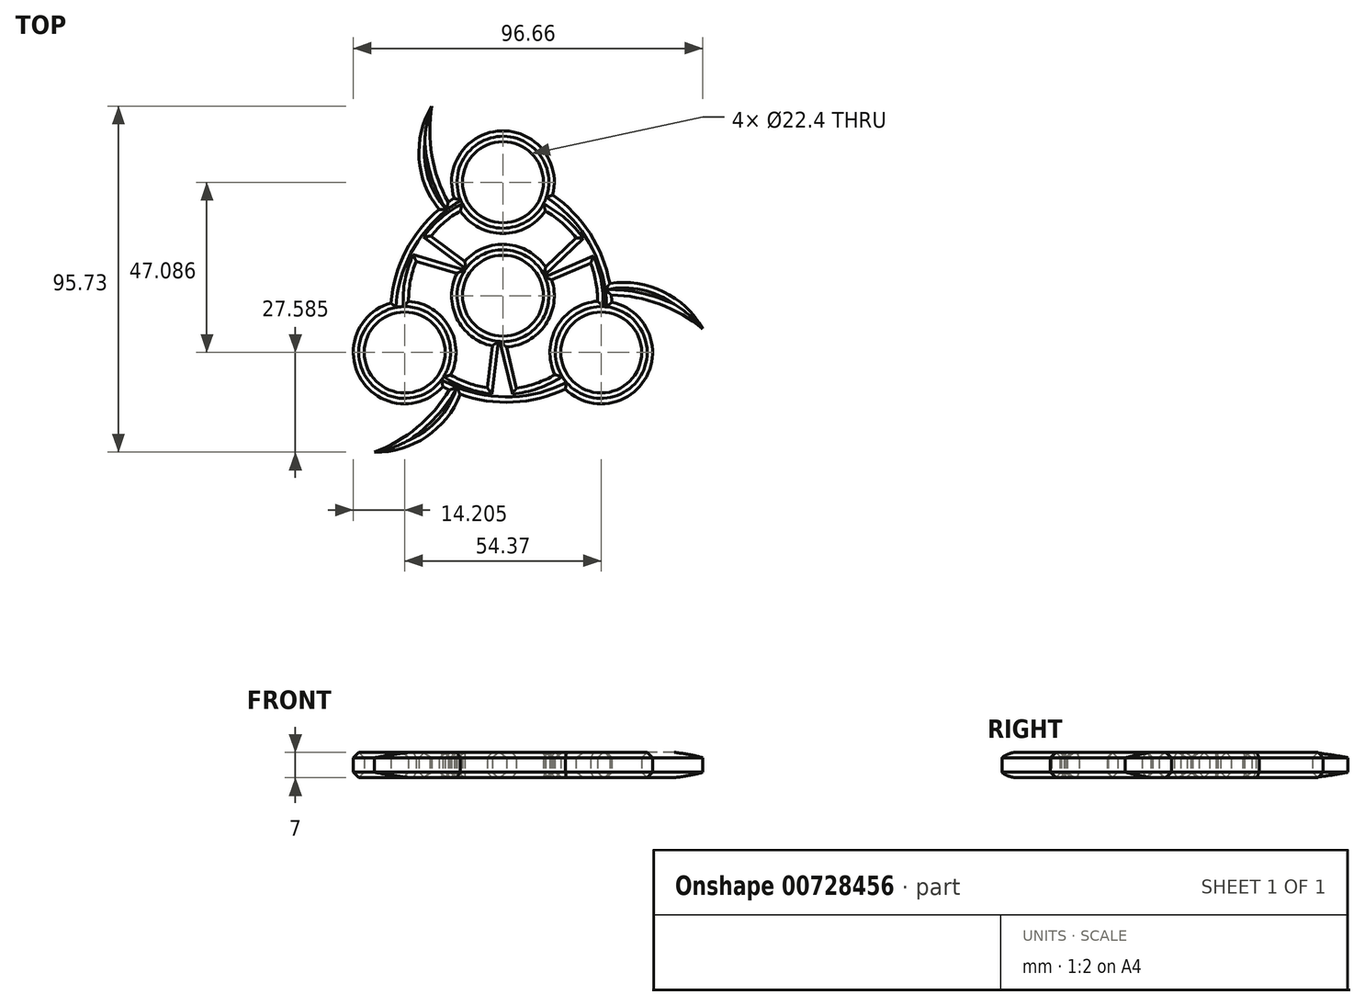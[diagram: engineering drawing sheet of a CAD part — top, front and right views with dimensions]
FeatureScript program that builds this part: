
annotation { "Feature Type Name" : "Feature", "Feature Type Description" : "" }
export const myFeature = defineFeature(function(context is Context, id is Id, definition is map)
    precondition{}
    {
        {
            var Q0;
            Q0=qCreatedBy(makeId("Top.planeOp"),FACE);
            var sketch = newSketch(context, id + "F0", { "sketchPlane" : qUnion([Q0])});
            skCircle(sketch, "E0", {"center": v(0, 0) * mm, "radius": 11.2 * mm});
            skArc(sketch, "E1", {"start": v(-12.76, 6.23) * mm, "mid": v(-12.77, -6.2) * mm, "end": v(-2.98, -13.88) * mm});
            skCircle(sketch, "E2", {"center": v(0, 31.4) * mm, "radius": 11.2 * mm});
            skArc(sketch, "E3", {"start": v(-11.77, 23.45) * mm, "mid": v(-0.04, 17.2) * mm, "end": v(11.72, 23.38) * mm});
            skCircle(sketch, "E4.1.0", {"center": v(-27.19, -15.7) * mm, "radius": 11.2 * mm});
            skArc(sketch, "E4.1.1", {"start": v(-14.42, -21.92) * mm, "mid": v(-14.87, -8.63) * mm, "end": v(-26.11, -1.54) * mm});
            skCircle(sketch, "E4.2.0", {"center": v(27.19, -15.7) * mm, "radius": 11.2 * mm});
            skArc(sketch, "E4.2.1", {"start": v(17.24, -25.83) * mm, "mid": v(38.73, -7.43) * mm, "end": v(14.39, -21.84) * mm});
            skArc(sketch, "E5", {"start": v(30.1, -1.8) * mm, "mid": v(30.05, -0.8) * mm, "end": v(29.97, 0.2) * mm});
            skArc(sketch, "E6", {"start": v(26.2, -1.53) * mm, "mid": v(22.35, 12.9) * mm, "end": v(11.72, 23.38) * mm});
            skArc(sketch, "E7.1.0", {"start": v(-11.77, 23.45) * mm, "mid": v(-22.34, 12.9) * mm, "end": v(-26.11, -1.54) * mm});
            skArc(sketch, "E7.1.1", {"start": v(-13.5, 26.97) * mm, "mid": v(-14.33, 26.43) * mm, "end": v(-15.15, 25.86) * mm});
            skArc(sketch, "E7.2.0", {"start": v(-14.42, -21.92) * mm, "mid": v(0, -25.8) * mm, "end": v(14.39, -21.84) * mm});
            skArc(sketch, "E7.2.1", {"start": v(-16.61, -25.18) * mm, "mid": v(-15.72, -25.63) * mm, "end": v(-14.82, -26.05) * mm});
            skLineSegment(sketch, "E8", {"start": v(-19.89, 16.5) * mm, "end": v(-10.53, 9.53) * mm});
            skLineSegment(sketch, "E9", {"start": v(-10.53, 9.53) * mm, "end": v(-12.76, 6.23) * mm});
            skLineSegment(sketch, "E10", {"start": v(-12.76, 6.23) * mm, "end": v(-24, 9.53) * mm});
            skLineSegment(sketch, "E11.1.0", {"start": v(-4.35, -25.48) * mm, "end": v(-2.98, -13.88) * mm});
            skLineSegment(sketch, "E11.1.1", {"start": v(0.98, -14.17) * mm, "end": v(3.75, -25.54) * mm});
            skLineSegment(sketch, "E11.2.0", {"start": v(24.24, 8.97) * mm, "end": v(13.51, 4.36) * mm});
            skLineSegment(sketch, "E11.2.1", {"start": v(11.78, 7.94) * mm, "end": v(20.25, 16.02) * mm});
            skArc(sketch, "E12.trimOffspring", {"start": v(11.78, 7.94) * mm, "mid": v(1, 14.16) * mm, "end": v(-10.53, 9.53) * mm});
            skArc(sketch, "E13.trimOffspring", {"start": v(0.98, -14.17) * mm, "mid": v(11.76, -7.96) * mm, "end": v(13.51, 4.36) * mm});
            skArc(sketch, "E14.trimOffspring", {"start": v(-31, -2.02) * mm, "mid": v(-39.25, -23.19) * mm, "end": v(-16.61, -25.18) * mm});
            skArc(sketch, "E15.trimOffspring", {"start": v(13.75, 27.85) * mm, "mid": v(-0.46, 45.58) * mm, "end": v(-13.5, 26.97) * mm});
            skArc(sketch, "E16", {"start": v(-19.69, 52.45) * mm, "mid": v(-23.19, 37.85) * mm, "end": v(-17.68, 23.9) * mm});
            skArc(sketch, "E17", {"start": v(-19.69, 52.45) * mm, "mid": v(-19.67, 38.77) * mm, "end": v(-15.15, 25.86) * mm});
            skArc(sketch, "E18.1.0", {"start": v(-35.58, -43.28) * mm, "mid": v(-21.19, -39) * mm, "end": v(-11.85, -27.25) * mm});
            skArc(sketch, "E18.1.1", {"start": v(-35.58, -43.28) * mm, "mid": v(-23.74, -36.42) * mm, "end": v(-14.82, -26.05) * mm});
            skArc(sketch, "E18.2.0", {"start": v(55.27, -9.18) * mm, "mid": v(44.38, 1.15) * mm, "end": v(29.53, 3.36) * mm});
            skArc(sketch, "E18.2.1", {"start": v(55.27, -9.18) * mm, "mid": v(43.41, -2.35) * mm, "end": v(29.97, 0.2) * mm});
            skArc(sketch, "E19.trimOffspring", {"start": v(-17.68, 23.9) * mm, "mid": v(-26.9, 12.26) * mm, "end": v(-31, -2.02) * mm});
            skArc(sketch, "E20.trimOffspring", {"start": v(-11.85, -27.25) * mm, "mid": v(2.84, -29.43) * mm, "end": v(17.24, -25.83) * mm});
            skArc(sketch, "E21.trimOffspring", {"start": v(29.53, 3.36) * mm, "mid": v(24.07, 17.17) * mm, "end": v(13.75, 27.85) * mm});
            skSolve(sketch);
        }
        {
            var Q0;
            {var subQ0=sQuery(id+"F0.wireOp",EDGE,"E7.1.0");Q0=makeQuery(id+"F0.imprint","IMPRINT",FACE,{"disambiguationData":[TD([[makeQuery(id+"F0.imprint","IMPRINT",EDGE,{"derivedFrom":subQ0}),-1.0]])]});}
            var Q1;
            {var subQ0=sQuery(id+"F0.wireOp",EDGE,"E5");Q1=makeQuery(id+"F0.imprint","IMPRINT",FACE,{"disambiguationData":[TD([[makeQuery(id+"F0.imprint","IMPRINT",EDGE,{"derivedFrom":subQ0}),1.0]])]});}
            var Q2;
            {var subQ0=sQuery(id+"F0.wireOp",EDGE,"E7.2.0");Q2=makeQuery(id+"F0.imprint","IMPRINT",FACE,{"disambiguationData":[TD([[makeQuery(id+"F0.imprint","IMPRINT",EDGE,{"derivedFrom":subQ0}),-1.0]])]});}
            var Q3;
            Q3=makeQuery(id+"F0.imprint","IMPRINT",FACE,{"disambiguationData":[TD([[makeQuery(id+"F0.imprint","IMPRINT",EDGE,{"derivedFrom":sQuery(id+"F0.wireOp",EDGE,"E4.2.0")}),-1.0]])]});
            var Q4;
            Q4=makeQuery(id+"F0.imprint","IMPRINT",FACE,{"disambiguationData":[TD([[makeQuery(id+"F0.imprint","IMPRINT",EDGE,{"derivedFrom":sQuery(id+"F0.wireOp",EDGE,"E4.1.0")}),-1.0]])]});
            var Q5;
            Q5=makeQuery(id+"F0.imprint","IMPRINT",FACE,{"disambiguationData":[TD([[makeQuery(id+"F0.imprint","IMPRINT",EDGE,{"derivedFrom":sQuery(id+"F0.wireOp",EDGE,"E2")}),-1.0]])]});
            var Q6;
            Q6=makeQuery(id+"F0.imprint","IMPRINT",FACE,{"disambiguationData":[TD([[makeQuery(id+"F0.imprint","IMPRINT",EDGE,{"derivedFrom":sQuery(id+"F0.wireOp",EDGE,"E0")}),-1.0]])]});
            var Q7;
            {var subQ1=sQuery(id+"F0.wireOp",EDGE,"E8");Q7=makeQuery(id+"F0.imprint","IMPRINT",FACE,{"disambiguationData":[TD([[makeQuery(id+"F0.imprint","IMPRINT",EDGE,{"derivedFrom":subQ1}),-1.0]])]});}
            var Q8;
            {var subQ0=sQuery(id+"F0.wireOp",EDGE,"E11.2.0");Q8=makeQuery(id+"F0.imprint","IMPRINT",FACE,{"disambiguationData":[TD([[makeQuery(id+"F0.imprint","IMPRINT",EDGE,{"derivedFrom":subQ0}),-1.0]])]});}
            var Q9;
            {var subQ0=sQuery(id+"F0.wireOp",EDGE,"E11.1.0");Q9=makeQuery(id+"F0.imprint","IMPRINT",FACE,{"disambiguationData":[TD([[makeQuery(id+"F0.imprint","IMPRINT",EDGE,{"derivedFrom":subQ0}),-1.0]])]});}
            extrude(context, id + "F1", {"entities" : qUnion([Q0, Q1, Q2, Q3, Q4, Q5, Q6, Q7, Q8, Q9]), "depth" : 7 * mm, "offsetDistance" : 25 * mm});
        }
        {
            var Q0;
            Q0=makeQuery(id+"F1.opExtrude","CAP_FACE",FACE,{"disambiguationData":[OSD([sQuery(id+"F0.wireOp",EDGE,"E0"),sQuery(id+"F0.wireOp",EDGE,"E1"),sQuery(id+"F0.wireOp",EDGE,"E2"),sQuery(id+"F0.wireOp",EDGE,"E3"),sQuery(id+"F0.wireOp",EDGE,"E4.1.0"),sQuery(id+"F0.wireOp",EDGE,"E4.1.1"),sQuery(id+"F0.wireOp",EDGE,"E4.2.0"),sQuery(id+"F0.wireOp",EDGE,"E4.2.1"),sQuery(id+"F0.wireOp",EDGE,"E5"),sQuery(id+"F0.wireOp",EDGE,"E6"),sQuery(id+"F0.wireOp",EDGE,"E7.1.0"),sQuery(id+"F0.wireOp",EDGE,"E7.1.1"),sQuery(id+"F0.wireOp",EDGE,"E7.2.0"),sQuery(id+"F0.wireOp",EDGE,"E7.2.1"),sQuery(id+"F0.wireOp",EDGE,"E8"),sQuery(id+"F0.wireOp",EDGE,"E10"),sQuery(id+"F0.wireOp",EDGE,"E11.1.0"),sQuery(id+"F0.wireOp",EDGE,"E11.1.1"),sQuery(id+"F0.wireOp",EDGE,"E11.2.0"),sQuery(id+"F0.wireOp",EDGE,"E11.2.1"),sQuery(id+"F0.wireOp",EDGE,"E12.trimOffspring"),sQuery(id+"F0.wireOp",EDGE,"E13.trimOffspring"),sQuery(id+"F0.wireOp",EDGE,"E14.trimOffspring"),sQuery(id+"F0.wireOp",EDGE,"E15.trimOffspring"),sQuery(id+"F0.wireOp",EDGE,"E16"),sQuery(id+"F0.wireOp",EDGE,"E17"),sQuery(id+"F0.wireOp",EDGE,"E18.1.0"),sQuery(id+"F0.wireOp",EDGE,"E18.1.1"),sQuery(id+"F0.wireOp",EDGE,"E18.2.0"),sQuery(id+"F0.wireOp",EDGE,"E18.2.1"),sQuery(id+"F0.wireOp",EDGE,"E19.trimOffspring"),sQuery(id+"F0.wireOp",EDGE,"E20.trimOffspring"),sQuery(id+"F0.wireOp",EDGE,"E21.trimOffspring")])],"isStart":false});
            var Q1;
            Q1=makeQuery(id+"F1.opExtrude","CAP_FACE",FACE,{"disambiguationData":[OSD([sQuery(id+"F0.wireOp",EDGE,"E0"),sQuery(id+"F0.wireOp",EDGE,"E1"),sQuery(id+"F0.wireOp",EDGE,"E2"),sQuery(id+"F0.wireOp",EDGE,"E3"),sQuery(id+"F0.wireOp",EDGE,"E4.1.0"),sQuery(id+"F0.wireOp",EDGE,"E4.1.1"),sQuery(id+"F0.wireOp",EDGE,"E4.2.0"),sQuery(id+"F0.wireOp",EDGE,"E4.2.1"),sQuery(id+"F0.wireOp",EDGE,"E5"),sQuery(id+"F0.wireOp",EDGE,"E6"),sQuery(id+"F0.wireOp",EDGE,"E7.1.0"),sQuery(id+"F0.wireOp",EDGE,"E7.1.1"),sQuery(id+"F0.wireOp",EDGE,"E7.2.0"),sQuery(id+"F0.wireOp",EDGE,"E7.2.1"),sQuery(id+"F0.wireOp",EDGE,"E8"),sQuery(id+"F0.wireOp",EDGE,"E10"),sQuery(id+"F0.wireOp",EDGE,"E11.1.0"),sQuery(id+"F0.wireOp",EDGE,"E11.1.1"),sQuery(id+"F0.wireOp",EDGE,"E11.2.0"),sQuery(id+"F0.wireOp",EDGE,"E11.2.1"),sQuery(id+"F0.wireOp",EDGE,"E12.trimOffspring"),sQuery(id+"F0.wireOp",EDGE,"E13.trimOffspring"),sQuery(id+"F0.wireOp",EDGE,"E14.trimOffspring"),sQuery(id+"F0.wireOp",EDGE,"E15.trimOffspring"),sQuery(id+"F0.wireOp",EDGE,"E16"),sQuery(id+"F0.wireOp",EDGE,"E17"),sQuery(id+"F0.wireOp",EDGE,"E18.1.0"),sQuery(id+"F0.wireOp",EDGE,"E18.1.1"),sQuery(id+"F0.wireOp",EDGE,"E18.2.0"),sQuery(id+"F0.wireOp",EDGE,"E18.2.1"),sQuery(id+"F0.wireOp",EDGE,"E19.trimOffspring"),sQuery(id+"F0.wireOp",EDGE,"E20.trimOffspring"),sQuery(id+"F0.wireOp",EDGE,"E21.trimOffspring")])],"isStart":true});
            chamfer(context, id + "F2", {"entities" : qUnion([Q0, Q1]), "width" : 1.5 * mm, "tangentPropagation" : true});
        }
    });
